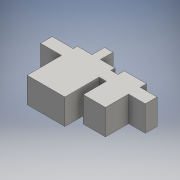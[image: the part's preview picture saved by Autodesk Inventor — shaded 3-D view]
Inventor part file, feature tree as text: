
AUTODESK INVENTOR PART (.ipt)
format: ipt  version: 2016 (Build 200138000, 138)  size: 120,832 bytes
history: native  units: mm
features: extrude x1, sketch x1
ambient origin geometry x8: Origin, YZ Plane, XZ Plane, XY Plane, X Axis, Y Axis, Z Axis, Center Point
bodies: Solid1 (feature_tree)
feature tree (2):
  extrude  "Extrusion1"  Depth=53.0mm
  sketch  "Sketch1"  dims[d0=90.0mm d1=53.0mm d2=17.0mm d3=40.0mm d4=50.0mm d5=10.0mm d6=15.0mm d9=28.0mm d10=110.0mm d11=83.0mm d12=61.0mm d13=0.0mm d14=30.0mm d15=20.0mm]
